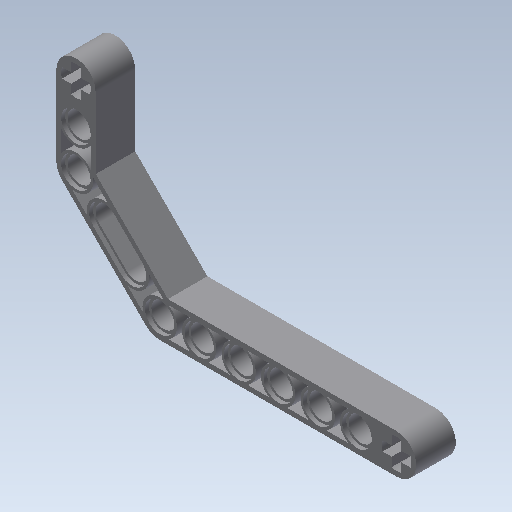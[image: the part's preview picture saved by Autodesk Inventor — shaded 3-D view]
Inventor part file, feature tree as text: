
AUTODESK INVENTOR PART (.ipt)
format: ipt  version: 2020 (Build 240168000, 168)  size: 428,544 bytes
history: native  units: mm
features: extrude x9, sketch x9
ambient origin geometry x8: Origin, YZ Plane, XZ Plane, XY Plane, X Axis, Y Axis, Z Axis, Center Point
bodies: Solid1 (feature_tree)
feature tree (18):
  extrude  "Extrusion1"  Depth=16.0mm
  extrude  "Extrusion2"  Depth=4.0mm
  extrude  "Extrusion3"  Depth=4.0mm
  extrude  "Extrusion4"  TaperAngle=135.0deg  [1 undecoded]
  extrude  "Extrusion5"  Depth=4.0mm
  extrude  "Extrusion6"  Depth=4.0mm
  extrude  "Extrusion7"  Depth=24.0mm
  extrude  "Extrusion8"  Depth=4.0mm
  extrude  "Extrusion9"  Depth=8.0mm
  sketch  "Sketch1"  dims[d2=8.0mm d4=48.0mm d6=16.0mm]
  sketch  "Sketch2"  dims[d9=24.0mm d12=4.0mm]
  sketch  "Sketch3"  dims[d13=4.0mm d14=4.0mm]
  sketch  "Sketch4"  dims[d15=4.0mm d16=135.0deg]
  sketch  "Sketch5"  dims[d17=135.0deg d18=4.0mm]
  sketch  "Sketch6"  dims[d19=4.0mm d20=4.0mm]
  sketch  "Sketch7"  dims[d21=4.0mm d22=24.0mm]
  sketch  "Sketch8"  dims[d23=0.0mm d25=4.0mm]
  sketch  "Sketch9"  dims[d26=4.0mm d27=8.0mm d28=8.0mm d29=22.343146mm d30=36.970563mm d31=8.0mm d32=0.0mm d33=6.0mm d34=3.0mm d35=3.0mm d36=3.0mm d37=3.0mm d38=2.0mm d39=2.0mm d40=2.0mm d41=2.0mm d42=1.0mm d43=1.0mm d44=1.0mm d45=1.0mm d46=10.0mm d47=0.0mm d48=6.0mm d49=3.0mm d50=2.0mm d51=3.0mm d52=2.0mm d53=3.0mm d54=2.0mm d55=3.0mm d56=2.0mm d57=1.0mm d58=1.0mm d59=1.0mm d60=1.0mm d61=10.0mm d62=0.0mm d63=5.0mm d64=10.0mm d66=10.0mm d67=60.0mm d69=8.0mm d71=10.0mm d72=0.0mm d74=5.0mm d75=10.0mm d77=10.0mm d78=20.0mm d80=8.0mm d82=10.0mm d83=0.0mm d111=2.5mm d112=2.5mm d115=0.0mm d116=4.0mm d117=5.0mm d118=2.5mm d119=8.0mm d120=8.0mm d121=10.0mm d122=0.0mm d123=6.0mm d124=6.0mm d125=6.0mm d126=6.0mm d127=6.0mm d128=6.0mm d129=3.0mm d130=6.0mm d131=6.0mm d132=0.8mm d133=0.0mm d134=6.0mm d135=6.0mm d136=6.0mm d137=6.0mm d138=6.0mm d139=6.0mm d140=6.0mm d141=6.0mm d142=3.0mm d143=0.8mm d144=0.0mm d145=7.0mm d146=7.0mm d147=7.0mm d148=7.0mm d149=7.0mm d151=3.5mm d152=3.5mm d153=3.5mm d154=3.5mm d155=4.394449mm d156=3.5mm d157=3.5mm d158=3.5mm d159=3.5mm d160=3.5mm d161=7.0mm d163=7.0mm d164=7.0mm d165=7.0mm d166=3.5mm d167=3.5mm d168=3.5mm d169=4.391753mm d170=10.0mm d171=0.0mm]
note: 1 required parameter value undecoded (feature->parameter linkage not recoverable at this tier; creation-order binding heuristic only, values carry confidence <= 0.55)
